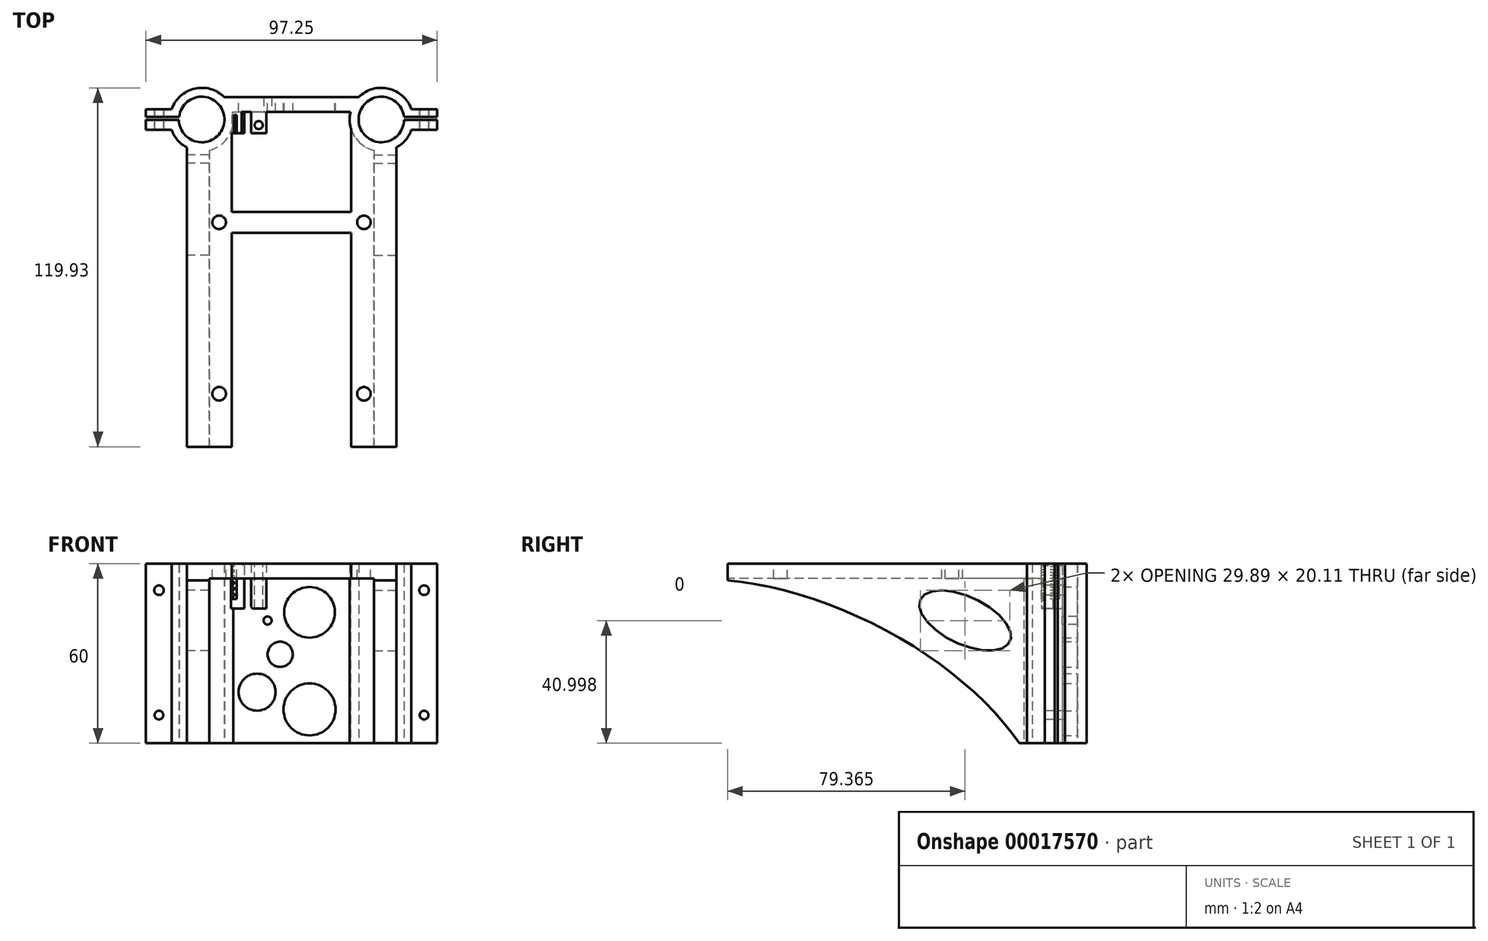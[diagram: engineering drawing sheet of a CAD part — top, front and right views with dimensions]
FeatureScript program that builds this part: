
annotation { "Feature Type Name" : "Feature", "Feature Type Description" : "" }
export const myFeature = defineFeature(function(context is Context, id is Id, definition is map)
    precondition{}
    {
        {
            var Q0;
            Q0=qCreatedBy(makeId("Top.planeOp"),FACE);
            var sketch = newSketch(context, id + "F0", { "sketchPlane" : qUnion([Q0])});
            skLineSegment(sketch, "E0.bottom", {"start": v(-17.98, 0) * mm, "end": v(1.72, 0) * mm});
            skLineSegment(sketch, "E0.top", {"start": v(-20.77, 5) * mm, "end": v(1.72, 5) * mm});
            skLineSegment(sketch, "E0.right", {"start": v(1.72, 5) * mm, "end": v(1.72, 0) * mm});
            skLineSegment(sketch, "E1.top", {"start": v(-33.28, -111.81) * mm, "end": v(-25.78, -111.81) * mm});
            skLineSegment(sketch, "E1.left", {"start": v(-33.28, -11.81) * mm, "end": v(-33.28, -111.81) * mm});
            skLineSegment(sketch, "E1.right", {"start": v(-25.78, -12.77) * mm, "end": v(-25.78, -111.81) * mm});
            skLineSegment(sketch, "E2", {"start": v(-38.32, 0.93) * mm, "end": v(-46.91, 0.93) * mm});
            skLineSegment(sketch, "E3", {"start": v(-46.91, -5.86) * mm, "end": v(-38.32, -5.86) * mm});
            skCircle(sketch, "E4", {"center": v(-28.28, -2.47) * mm, "radius": 7.6 * mm});
            skCircle(sketch, "E5", {"center": v(-28.28, -2.47) * mm, "radius": 10.6 * mm});
            skLineSegment(sketch, "E6", {"start": v(-46.91, 0.93) * mm, "end": v(-46.91, -5.86) * mm});
            skLineSegment(sketch, "E7", {"start": v(-27.79, 8.11) * mm, "end": v(-27.79, 5.11) * mm});
            skLineSegment(sketch, "E8", {"start": v(-28.28, -2.47) * mm, "end": v(-28.28, -16.23) * mm, "construction": true});
            skSolve(sketch);
        }
        {
            var Q0;
            {var subQ4=sQuery(id+"F0.wireOp",EDGE,"E0.bottom");Q0=makeQuery(id+"F0.imprint","IMPRINT",FACE,{"disambiguationData":[TD([[makeQuery(id+"F0.imprint","IMPRINT",EDGE,{"derivedFrom":subQ4}),1.0]])]});}
            var Q1;
            Q1=makeQuery(id+"F0.imprint","IMPRINT",FACE,{"disambiguationData":[TD([[makeQuery(id+"F0.imprint","IMPRINT",EDGE,{"derivedFrom":sQuery(id+"F0.wireOp",EDGE,"E1.top")}),1.0]])]});
            var Q2;
            Q2=makeQuery(id+"F0.imprint","IMPRINT",FACE,{"disambiguationData":[TD([[makeQuery(id+"F0.imprint","IMPRINT",EDGE,{"derivedFrom":sQuery(id+"F0.wireOp",EDGE,"E4")}),-1.0]])]});
            var Q3;
            {var subQ2=sQuery(id+"F0.wireOp",EDGE,"E2");Q3=makeQuery(id+"F0.imprint","IMPRINT",FACE,{"disambiguationData":[TD([[makeQuery(id+"F0.imprint","IMPRINT",EDGE,{"derivedFrom":subQ2}),1.0]])]});}
            extrude(context, id + "F1", {"entities" : qUnion([Q0, Q1, Q2, Q3]), "depth" : 60 * mm});
        }
        {
            var Q0;
            Q0=makeQuery(id+"F1.opExtrude","SWEPT_FACE",FACE,{"disambiguationData":[OSD([sQuery(id+"F0.wireOp",EDGE,"E1.left")])]});
            var sketch = newSketch(context, id + "F2", { "sketchPlane" : qUnion([Q0])});
            skEllipse(sketch, "E9", {"center": v(82.4, 0) * mm, "majorRadius": 84.12 * mm, "minorRadius": 44.3 * mm, "majorAxis": v(0.9, 0.45)});
            skSolve(sketch);
        }
        {
            var Q0;
            {var subQ0=makeQuery(id+"F1.opExtrude","SWEPT_FACE",FACE,{"disambiguationData":[OSD([sQuery(id+"F0.wireOp",EDGE,"E0.top")])]});Q0=makeQuery(id+"FiK1FXiIRTqYzcR_1.boolean.opBoolean","MERGE",FACE,{"derivedFrom":[subQ0,makeQuery(id+"FiK1FXiIRTqYzcR_1.opPattern","COPY",FACE,{"derivedFrom":subQ0,"instanceName":"1"})]});}
            var sketch = newSketch(context, id + "F3", { "sketchPlane" : qUnion([Q0])});
            skCircle(sketch, "E10", {"center": v(-7.72, 43.75) * mm, "radius": 8.46 * mm});
            skCircle(sketch, "E11", {"center": v(-7.72, 11.3) * mm, "radius": 8.68 * mm});
            skCircle(sketch, "E12", {"center": v(9.78, 17.06) * mm, "radius": 6.18 * mm});
            skCircle(sketch, "E13", {"center": v(2.08, 29.7) * mm, "radius": 4.21 * mm});
            skSolve(sketch);
        }
        {
            var Q0;
            Q0=qSketchRegion(id+"F2",true);
            extrude(context, id + "F4", {"entities" : qUnion([Q0]), "operationType" : NewBodyOperationType.REMOVE, "endBound" : BoundingType.THROUGH_ALL, "oppositeDirection" : true, "depth" : 25 * mm});
        }
        {
            var Q0;
            {var subQ0=makeQuery(id+"F1.opExtrude","CAP_FACE",FACE,{"disambiguationData":[OSD([sQuery(id+"F0.wireOp",EDGE,"E0.bottom"),sQuery(id+"F0.wireOp",EDGE,"E0.top"),sQuery(id+"F0.wireOp",EDGE,"E0.right"),sQuery(id+"F0.wireOp",EDGE,"E1.top"),sQuery(id+"F0.wireOp",EDGE,"E1.left"),sQuery(id+"F0.wireOp",EDGE,"E1.right"),sQuery(id+"F0.wireOp",EDGE,"E2"),sQuery(id+"F0.wireOp",EDGE,"E3"),sQuery(id+"F0.wireOp",EDGE,"E4"),sQuery(id+"F0.wireOp",EDGE,"E5"),sQuery(id+"F0.wireOp",EDGE,"E6")])],"isStart":false});Q0=makeQuery(id+"FiK1FXiIRTqYzcR_1.boolean.opBoolean","MERGE",FACE,{"derivedFrom":[subQ0,makeQuery(id+"FiK1FXiIRTqYzcR_1.opPattern","COPY",FACE,{"derivedFrom":subQ0,"instanceName":"1"})]});}
            var sketch = newSketch(context, id + "F5", { "sketchPlane" : qUnion([Q0])});
            skLineSegment(sketch, "E14", {"start": v(-30.19, -111.81) * mm, "end": v(-28.68, -12.77) * mm});
            skLineSegment(sketch, "E15", {"start": v(-18.19, -5.68) * mm, "end": v(-18.19, -111.81) * mm});
            skLineSegment(sketch, "E16", {"start": v(-30.19, -111.81) * mm, "end": v(-18.19, -111.81) * mm});
            skLineSegment(sketch, "E17", {"start": v(-28.68, -12.77) * mm, "end": v(-18.19, -5.68) * mm});
            skCircle(sketch, "E18", {"center": v(-22.45, -36.81) * mm, "radius": 2.27 * mm});
            skCircle(sketch, "E19", {"center": v(-22.45, -94.08) * mm, "radius": 2.27 * mm});
            skLineSegment(sketch, "E20.bottom", {"start": v(-18.19, -33.31) * mm, "end": v(4.26, -33.31) * mm});
            skLineSegment(sketch, "E20.top", {"start": v(-18.19, -40.31) * mm, "end": v(4.26, -40.31) * mm});
            skLineSegment(sketch, "E20.left", {"start": v(-18.19, -33.31) * mm, "end": v(-18.19, -40.31) * mm});
            skLineSegment(sketch, "E20.right", {"start": v(4.26, -33.31) * mm, "end": v(4.26, -40.31) * mm});
            skPoint(sketch, "E21", {"position": v(4.26, -36.81) * mm});
            skSolve(sketch);
        }
        {
            var Q0;
            Q0=qSketchRegion(id+"F5",true);
            extrude(context, id + "F6", {"entities" : qUnion([Q0]), "oppositeDirection" : true, "depth" : 5 * mm});
        }
        {
            var Q0;
            Q0=makeQuery(id+"F1.opExtrude","SWEPT_BODY",BODY,{"disambiguationData":[OSD([sQuery(id+"F0.wireOp",EDGE,"E0.bottom"),sQuery(id+"F0.wireOp",EDGE,"E0.top"),sQuery(id+"F0.wireOp",EDGE,"E0.right"),sQuery(id+"F0.wireOp",EDGE,"E1.top"),sQuery(id+"F0.wireOp",EDGE,"E1.left"),sQuery(id+"F0.wireOp",EDGE,"E1.right"),sQuery(id+"F0.wireOp",EDGE,"E2"),sQuery(id+"F0.wireOp",EDGE,"E3"),sQuery(id+"F0.wireOp",EDGE,"E4"),sQuery(id+"F0.wireOp",EDGE,"E5"),sQuery(id+"F0.wireOp",EDGE,"E6")])]});
            var Q1;
            Q1=makeQuery(id+"F6.opExtrude","SWEPT_BODY",BODY,{"disambiguationData":[OSD([sQuery(id+"F5.wireOp",EDGE,"E14"),sQuery(id+"F5.wireOp",EDGE,"E15"),sQuery(id+"F5.wireOp",EDGE,"E16"),sQuery(id+"F5.wireOp",EDGE,"E17")])]});
            booleanBodies(context, id + "F7", {"operationType" : BooleanOperationType.UNION, "tools" : qUnion([Q0, Q1])});
        }
        {
            var Q0;
            {var subQ0=makeQuery(id+"F7.opBoolean","MERGE",FACE,{"derivedFrom":[makeQuery(id+"F1.opExtrude","CAP_FACE",FACE,{"disambiguationData":[OSD([sQuery(id+"F0.wireOp",EDGE,"E0.bottom"),sQuery(id+"F0.wireOp",EDGE,"E0.top"),sQuery(id+"F0.wireOp",EDGE,"E0.right"),sQuery(id+"F0.wireOp",EDGE,"E1.top"),sQuery(id+"F0.wireOp",EDGE,"E1.left"),sQuery(id+"F0.wireOp",EDGE,"E1.right"),sQuery(id+"F0.wireOp",EDGE,"E2"),sQuery(id+"F0.wireOp",EDGE,"E3"),sQuery(id+"F0.wireOp",EDGE,"E4"),sQuery(id+"F0.wireOp",EDGE,"E5"),sQuery(id+"F0.wireOp",EDGE,"E6")])],"isStart":false}),makeQuery(id+"F6.opExtrude","CAP_FACE",FACE,{"disambiguationData":[OSD([sQuery(id+"F5.wireOp",EDGE,"E14"),sQuery(id+"F5.wireOp",EDGE,"E15"),sQuery(id+"F5.wireOp",EDGE,"E16"),sQuery(id+"F5.wireOp",EDGE,"E17"),sQuery(id+"F5.wireOp",EDGE,"E18"),sQuery(id+"F5.wireOp",EDGE,"E19")])],"isStart":true})]});Q0=makeQuery(id+"F12.boolean.opBoolean","MERGE",FACE,{"derivedFrom":[subQ0,makeQuery(id+"F12.opPattern","COPY",FACE,{"derivedFrom":subQ0,"instanceName":"1"})]});}
            var sketch = newSketch(context, id + "F8", { "sketchPlane" : qUnion([Q0])});
            skLineSegment(sketch, "E22.bottom", {"start": v(-47.38, -1.55) * mm, "end": v(-35.44, -1.55) * mm});
            skLineSegment(sketch, "E22.top", {"start": v(-47.38, -2.55) * mm, "end": v(-35.44, -2.55) * mm});
            skLineSegment(sketch, "E22.left", {"start": v(-47.38, -1.55) * mm, "end": v(-47.38, -2.55) * mm});
            skLineSegment(sketch, "E22.right", {"start": v(-35.44, -1.55) * mm, "end": v(-35.44, -2.55) * mm});
            skSolve(sketch);
        }
        {
            var Q0;
            Q0=qSketchRegion(id+"F8",true);
            extrude(context, id + "F9", {"entities" : qUnion([Q0]), "operationType" : NewBodyOperationType.REMOVE, "endBound" : BoundingType.THROUGH_ALL, "oppositeDirection" : true, "depth" : 25 * mm});
        }
        {
            var Q0;
            Q0=makeQuery(id+"F1.opExtrude","SWEPT_FACE",FACE,{"disambiguationData":[OSD([sQuery(id+"F0.wireOp",EDGE,"E3")])]});
            var sketch = newSketch(context, id + "F10", { "sketchPlane" : qUnion([Q0])});
            skCircle(sketch, "E23", {"center": v(-42.56, 51.1) * mm, "radius": 1.6 * mm});
            skCircle(sketch, "E24", {"center": v(-42.56, 9.4) * mm, "radius": 1.45 * mm});
            skSolve(sketch);
        }
        {
            var Q0;
            Q0=qSketchRegion(id+"F10",true);
            extrude(context, id + "F11", {"entities" : qUnion([Q0]), "operationType" : NewBodyOperationType.REMOVE, "endBound" : BoundingType.THROUGH_ALL, "oppositeDirection" : true, "depth" : 25 * mm});
        }
        {
            var Q0;
            Q0=makeQuery(id+"F1.opExtrude","SWEPT_BODY",BODY,{"disambiguationData":[OSD([sQuery(id+"F0.wireOp",EDGE,"E0.bottom"),sQuery(id+"F0.wireOp",EDGE,"E0.top"),sQuery(id+"F0.wireOp",EDGE,"E0.right"),sQuery(id+"F0.wireOp",EDGE,"E1.top"),sQuery(id+"F0.wireOp",EDGE,"E1.left"),sQuery(id+"F0.wireOp",EDGE,"E1.right"),sQuery(id+"F0.wireOp",EDGE,"E2"),sQuery(id+"F0.wireOp",EDGE,"E3"),sQuery(id+"F0.wireOp",EDGE,"E4"),sQuery(id+"F0.wireOp",EDGE,"E5"),sQuery(id+"F0.wireOp",EDGE,"E6")])]});
            var Q1;
            Q1=makeQuery(id+"F1.opExtrude","SWEPT_FACE",FACE,{"disambiguationData":[OSD([sQuery(id+"F0.wireOp",EDGE,"E0.right")])]});
            mirror(context, id + "F12", {"operationType" : NewBodyOperationType.ADD, "entities" : qUnion([Q0]), "mirrorPlane" : qUnion([Q1])});
        }
        {
            var Q0;
            Q0=qSketchRegion(id+"F3",true);
            extrude(context, id + "F13", {"entities" : qUnion([Q0]), "operationType" : NewBodyOperationType.REMOVE, "endBound" : BoundingType.THROUGH_ALL, "oppositeDirection" : true, "depth" : 25 * mm});
        }
        {
            var Q0;
            {var subQ0=makeQuery(id+"F1.opExtrude","SWEPT_FACE",FACE,{"disambiguationData":[OSD([sQuery(id+"F0.wireOp",EDGE,"E0.bottom")])]});Q0=makeQuery(id+"F12.boolean.opBoolean","MERGE",FACE,{"derivedFrom":[subQ0,makeQuery(id+"F12.opPattern","COPY",FACE,{"derivedFrom":subQ0,"instanceName":"1"})]});}
            var sketch = newSketch(context, id + "F14", { "sketchPlane" : qUnion([Q0])});
            skPoint(sketch, "E25", {"position": v(1.72, 60) * mm});
            skCircle(sketch, "E26", {"center": v(-6.28, 41) * mm, "radius": 1.35 * mm});
            skSolve(sketch);
        }
        {
            var Q0;
            Q0=qSketchRegion(id+"F14",true);
            extrude(context, id + "F15", {"entities" : qUnion([Q0]), "operationType" : NewBodyOperationType.REMOVE, "endBound" : BoundingType.THROUGH_ALL, "oppositeDirection" : true, "depth" : 25 * mm});
        }
        {
            var Q0;
            {var subQ0=makeQuery(id+"F1.opExtrude","SWEPT_FACE",FACE,{"disambiguationData":[OSD([sQuery(id+"F0.wireOp",EDGE,"E0.bottom")])]});Q0=makeQuery(id+"F12.boolean.opBoolean","MERGE",FACE,{"derivedFrom":[subQ0,makeQuery(id+"F12.opPattern","COPY",FACE,{"derivedFrom":subQ0,"instanceName":"1"})]});}
            var sketch = newSketch(context, id + "F16", { "sketchPlane" : qUnion([Q0])});
            skLineSegment(sketch, "E27.bottom", {"start": v(-18.45, 60) * mm, "end": v(-14.12, 60) * mm});
            skLineSegment(sketch, "E27.top", {"start": v(-18.45, 45) * mm, "end": v(-14.12, 45) * mm});
            skLineSegment(sketch, "E27.left", {"start": v(-18.45, 60) * mm, "end": v(-18.45, 45) * mm});
            skLineSegment(sketch, "E27.right", {"start": v(-14.12, 60) * mm, "end": v(-14.12, 45) * mm});
            skLineSegment(sketch, "E28.bottom", {"start": v(-11.72, 60) * mm, "end": v(-6.72, 60) * mm});
            skLineSegment(sketch, "E28.top", {"start": v(-11.72, 45) * mm, "end": v(-6.72, 45) * mm});
            skLineSegment(sketch, "E28.left", {"start": v(-11.72, 60) * mm, "end": v(-11.72, 45) * mm});
            skLineSegment(sketch, "E28.right", {"start": v(-6.72, 60) * mm, "end": v(-6.72, 45) * mm});
            skSolve(sketch);
        }
        {
            var Q0;
            Q0=qSketchRegion(id+"F16",true);
            extrude(context, id + "F17", {"entities" : qUnion([Q0]), "operationType" : NewBodyOperationType.ADD, "depth" : 7 * mm});
        }
        {
            var Q0;
            {var subQ0=makeQuery(id+"F7.opBoolean","MERGE",FACE,{"derivedFrom":[makeQuery(id+"F1.opExtrude","CAP_FACE",FACE,{"disambiguationData":[OSD([sQuery(id+"F0.wireOp",EDGE,"E0.bottom"),sQuery(id+"F0.wireOp",EDGE,"E0.top"),sQuery(id+"F0.wireOp",EDGE,"E0.right"),sQuery(id+"F0.wireOp",EDGE,"E1.top"),sQuery(id+"F0.wireOp",EDGE,"E1.left"),sQuery(id+"F0.wireOp",EDGE,"E1.right"),sQuery(id+"F0.wireOp",EDGE,"E2"),sQuery(id+"F0.wireOp",EDGE,"E3"),sQuery(id+"F0.wireOp",EDGE,"E4"),sQuery(id+"F0.wireOp",EDGE,"E5"),sQuery(id+"F0.wireOp",EDGE,"E6")])],"isStart":false}),makeQuery(id+"F6.opExtrude","CAP_FACE",FACE,{"disambiguationData":[OSD([sQuery(id+"F5.wireOp",EDGE,"E14"),sQuery(id+"F5.wireOp",EDGE,"E15"),sQuery(id+"F5.wireOp",EDGE,"E16"),sQuery(id+"F5.wireOp",EDGE,"E17"),sQuery(id+"F5.wireOp",EDGE,"E18"),sQuery(id+"F5.wireOp",EDGE,"E19")])],"isStart":true})]});Q0=makeQuery(id+"F17.boolean.opBoolean","MERGE",FACE,{"derivedFrom":[makeQuery(id+"F12.boolean.opBoolean","MERGE",FACE,{"derivedFrom":[subQ0,makeQuery(id+"F12.opPattern","COPY",FACE,{"derivedFrom":subQ0,"instanceName":"1"})]}),makeQuery(id+"F17.opExtrude","SWEPT_FACE",FACE,{"disambiguationData":[OSD([sQuery(id+"F16.wireOp",EDGE,"E27.bottom")])]}),makeQuery(id+"F17.opExtrude","SWEPT_FACE",FACE,{"disambiguationData":[OSD([sQuery(id+"F16.wireOp",EDGE,"E28.bottom")])]})]});}
            var sketch = newSketch(context, id + "F18", { "sketchPlane" : qUnion([Q0])});
            skCircle(sketch, "E29", {"center": v(-9.24, -4.35) * mm, "radius": 1.35 * mm});
            skPoint(sketch, "E30", {"position": v(-6.72, 0) * mm});
            skLineSegment(sketch, "E31", {"start": v(-6.72, 0) * mm, "end": v(-10.96, 0) * mm, "construction": true});
            skSolve(sketch);
        }
        {
            var Q0;
            Q0=qSketchRegion(id+"F18",true);
            extrude(context, id + "F19", {"entities" : qUnion([Q0]), "operationType" : NewBodyOperationType.REMOVE, "endBound" : BoundingType.THROUGH_ALL, "oppositeDirection" : true, "depth" : 25 * mm});
        }
        {
            var Q0;
            Q0=makeQuery(id+"F17.opExtrude","CAP_FACE",FACE,{"disambiguationData":[OSD([sQuery(id+"F16.wireOp",EDGE,"E27.bottom"),sQuery(id+"F16.wireOp",EDGE,"E27.top"),sQuery(id+"F16.wireOp",EDGE,"E27.left"),sQuery(id+"F16.wireOp",EDGE,"E27.right")])],"isStart":false});
            var sketch = newSketch(context, id + "F20", { "sketchPlane" : qUnion([Q0])});
            skLineSegment(sketch, "E32", {"start": v(-17.5, 60) * mm, "end": v(-17.5, 59) * mm});
            skLineSegment(sketch, "E33", {"start": v(-17.5, 59) * mm, "end": v(-18.3, 59) * mm});
            skLineSegment(sketch, "E34", {"start": v(-18.3, 59) * mm, "end": v(-18.3, 58) * mm});
            skLineSegment(sketch, "E35", {"start": v(-18.3, 58) * mm, "end": v(-17.48, 58) * mm});
            skLineSegment(sketch, "E36.1.0.0", {"start": v(-18.3, 56.02) * mm, "end": v(-17.48, 56.02) * mm});
            skLineSegment(sketch, "E36.1.0.1", {"start": v(-17.5, 57.02) * mm, "end": v(-18.3, 57.02) * mm});
            skLineSegment(sketch, "E36.1.0.2", {"start": v(-17.5, 58.02) * mm, "end": v(-17.5, 57.02) * mm});
            skLineSegment(sketch, "E36.1.0.3", {"start": v(-18.3, 57.02) * mm, "end": v(-18.3, 56.02) * mm});
            skLineSegment(sketch, "E36.2.0.0", {"start": v(-18.3, 54.05) * mm, "end": v(-17.48, 54.05) * mm});
            skLineSegment(sketch, "E36.2.0.1", {"start": v(-17.5, 55.05) * mm, "end": v(-18.3, 55.05) * mm});
            skLineSegment(sketch, "E36.2.0.2", {"start": v(-17.5, 56.05) * mm, "end": v(-17.5, 55.05) * mm});
            skLineSegment(sketch, "E36.2.0.3", {"start": v(-18.3, 55.05) * mm, "end": v(-18.3, 54.05) * mm});
            skLineSegment(sketch, "E36.3.0.0", {"start": v(-18.3, 52.07) * mm, "end": v(-17.48, 52.07) * mm});
            skLineSegment(sketch, "E36.3.0.1", {"start": v(-17.5, 53.07) * mm, "end": v(-18.3, 53.07) * mm});
            skLineSegment(sketch, "E36.3.0.2", {"start": v(-17.5, 54.07) * mm, "end": v(-17.5, 53.07) * mm});
            skLineSegment(sketch, "E36.3.0.3", {"start": v(-18.3, 53.07) * mm, "end": v(-18.3, 52.07) * mm});
            skLineSegment(sketch, "E36.4.0.0", {"start": v(-18.3, 50.1) * mm, "end": v(-17.48, 50.1) * mm});
            skLineSegment(sketch, "E36.4.0.1", {"start": v(-17.5, 51.1) * mm, "end": v(-18.3, 51.1) * mm});
            skLineSegment(sketch, "E36.4.0.2", {"start": v(-17.5, 52.1) * mm, "end": v(-17.5, 51.1) * mm});
            skLineSegment(sketch, "E36.4.0.3", {"start": v(-18.3, 51.1) * mm, "end": v(-18.3, 50.1) * mm});
            skLineSegment(sketch, "E36.5.0.0", {"start": v(-18.3, 48.12) * mm, "end": v(-17.48, 48.12) * mm});
            skLineSegment(sketch, "E36.5.0.1", {"start": v(-17.5, 49.12) * mm, "end": v(-18.3, 49.12) * mm});
            skLineSegment(sketch, "E36.5.0.2", {"start": v(-17.5, 50.12) * mm, "end": v(-17.5, 49.12) * mm});
            skLineSegment(sketch, "E36.5.0.3", {"start": v(-18.3, 49.12) * mm, "end": v(-18.3, 48.12) * mm});
            skLineSegment(sketch, "E36.direction1", {"start": v(-18.3, 58) * mm, "end": v(-18.3, 56.02) * mm, "construction": true});
            skLineSegment(sketch, "E37", {"start": v(-17.48, 48.12) * mm, "end": v(-16.6, 48.12) * mm});
            skLineSegment(sketch, "E38", {"start": v(-16.6, 48.12) * mm, "end": v(-16.6, 60) * mm});
            skLineSegment(sketch, "E39", {"start": v(-16.6, 60) * mm, "end": v(-17.5, 60) * mm});
            skSolve(sketch);
        }
        {
            var Q0;
            Q0=qSketchRegion(id+"F20",true);
            extrude(context, id + "F21", {"entities" : qUnion([Q0]), "operationType" : NewBodyOperationType.REMOVE, "oppositeDirection" : true, "depth" : 6 * mm});
        }
        {
            var Q0;
            Q0=makeQuery(id+"F17.opExtrude","SWEPT_EDGE",EDGE,{"disambiguationData":[OSD([sQuery(id+"F16.wireOp",EDGE,"E28.top"),sQuery(id+"F16.wireOp",EDGE,"E28.left")])]});
            fillet(context, id + "F22", {"entities" : qUnion([Q0]), "radius" : 0.7 * mm, "tangentPropagation" : true, "allowEdgeOverflow" : false});
        }
        {
            var Q0;
            Q0=makeQuery(id+"F17.opExtrude","SWEPT_EDGE",EDGE,{"disambiguationData":[OSD([sQuery(id+"F0.wireOp",EDGE,"E0.bottom"),sQuery(id+"F16.wireOp",EDGE,"E27.bottom"),sQuery(id+"F16.wireOp",EDGE,"E27.right")])]});
            chamfer(context, id + "F23", {"entities" : qUnion([Q0]), "width" : 0.8 * mm, "tangentPropagation" : true});
        }
        {
            var Q0;
            Q0=makeQuery(id+"F1.opExtrude","SWEPT_FACE",FACE,{"disambiguationData":[OSD([sQuery(id+"F0.wireOp",EDGE,"E1.left")])]});
            var sketch = newSketch(context, id + "F24", { "sketchPlane" : qUnion([Q0])});
            skEllipse(sketch, "E40", {"center": v(32.45, 41) * mm, "majorRadius": 16.52 * mm, "minorRadius": 7.95 * mm, "majorAxis": v(0.9, 0.43)});
            skSolve(sketch);
        }
        {
            var Q0;
            Q0=qSketchRegion(id+"F24",true);
            extrude(context, id + "F25", {"entities" : qUnion([Q0]), "operationType" : NewBodyOperationType.REMOVE, "endBound" : BoundingType.THROUGH_ALL, "oppositeDirection" : true, "depth" : 25 * mm});
        }
    });
